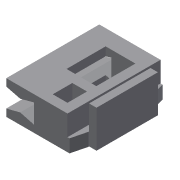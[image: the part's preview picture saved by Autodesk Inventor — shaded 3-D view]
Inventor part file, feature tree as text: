
AUTODESK INVENTOR PART (.ipt)
format: ipt  version: 2015 (Build 190159000, 159)  size: 158,208 bytes
history: native  units: mm
features: extrude x5, sketch x4, projected_geometry x4, chamfer x2
ambient origin geometry x8: Origin, YZ Plane, XZ Plane, XY Plane, X Axis, Y Axis, Z Axis, Center Point
bodies: 实体1 (feature_tree)
feature tree (15):
  sketch  "草图1"  dims[d0=18.0mm d1=40.0mm]
  extrude  "拉伸1"  Depth=40.0mm
  extrude  "拉伸2"  Depth=20.0mm
  extrude  "拉伸3"  Depth=15.0mm
  chamfer  "倒角1"  Distance=33.0mm
  chamfer  "倒角2"  Distance=50.0mm
  extrude  "拉伸4"  Depth=33.0mm
  extrude  "拉伸6"  Depth=11.0mm
  sketch  "草图2"  dims[d3=20.0mm d4=3.9mm]
  projected_geometry  "投影回路1"
  sketch  "草图3"  dims[d6=5.8mm d7=15.0mm d8=3.8mm]
  projected_geometry  "投影回路2"
  sketch  "草图4"  dims[d9=7.5mm d10=33.0mm d11=50.0mm d12=0.0mm d13=33.0mm d14=11.0mm d15=3.1mm d16=4.0mm d17=50.0mm d18=0.0mm d19=33.0mm d20=50.0mm d21=0.0mm d22=2.0mm d23=8.0mm d24=45.0deg d25=2.0mm d26=8.0mm d27=45.0deg d28=21.0mm d29=8.5mm d30=5.0mm d32=21.0mm d33=50.0mm d34=0.0mm d35=5.0mm d36=5.0mm d37=5.0mm d38=5.0mm d39=9.0mm d42=2.0mm d43=0.0mm]
  projected_geometry  "投影回路3"
  projected_geometry  "投影回路4"
